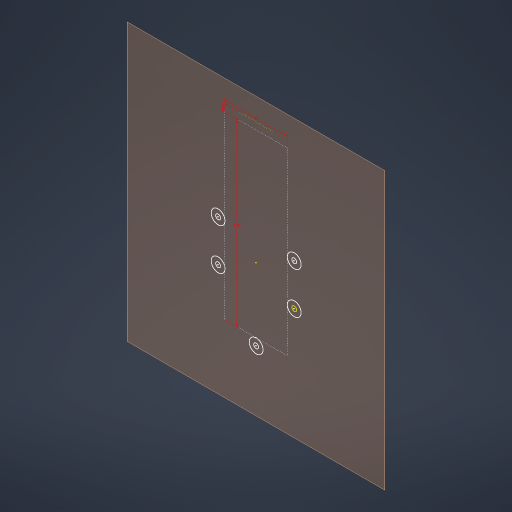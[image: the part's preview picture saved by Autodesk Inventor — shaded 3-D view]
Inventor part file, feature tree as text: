
AUTODESK INVENTOR PART (.ipt)
format: ipt  version: 2023 (Build 270158000, 158)  size: 167,424 bytes
history: native  units: mm
features: other x3, reference x2, plane x1, sketch x1
ambient origin geometry x8: Origin, YZ Plane, XZ Plane, XY Plane, X Axis, Y Axis, Z Axis, Center Point
feature tree (7):
  plane  "Work Plane3"
  sketch  "Sketch2"  dims[d0=45.0mm d1=130.0mm d3=5.0mm]
  reference  "Reference1"
  reference  "Reference2"
  parser-record x1  (decoder bookkeeping rows leaked as tree rows — omitted from the tree; the rows remain in map.json)
  other  "total.iam"
  other  "bottom:1"
note: 1 file-system path scrubbed to <path> (originals preserved in map.json)
